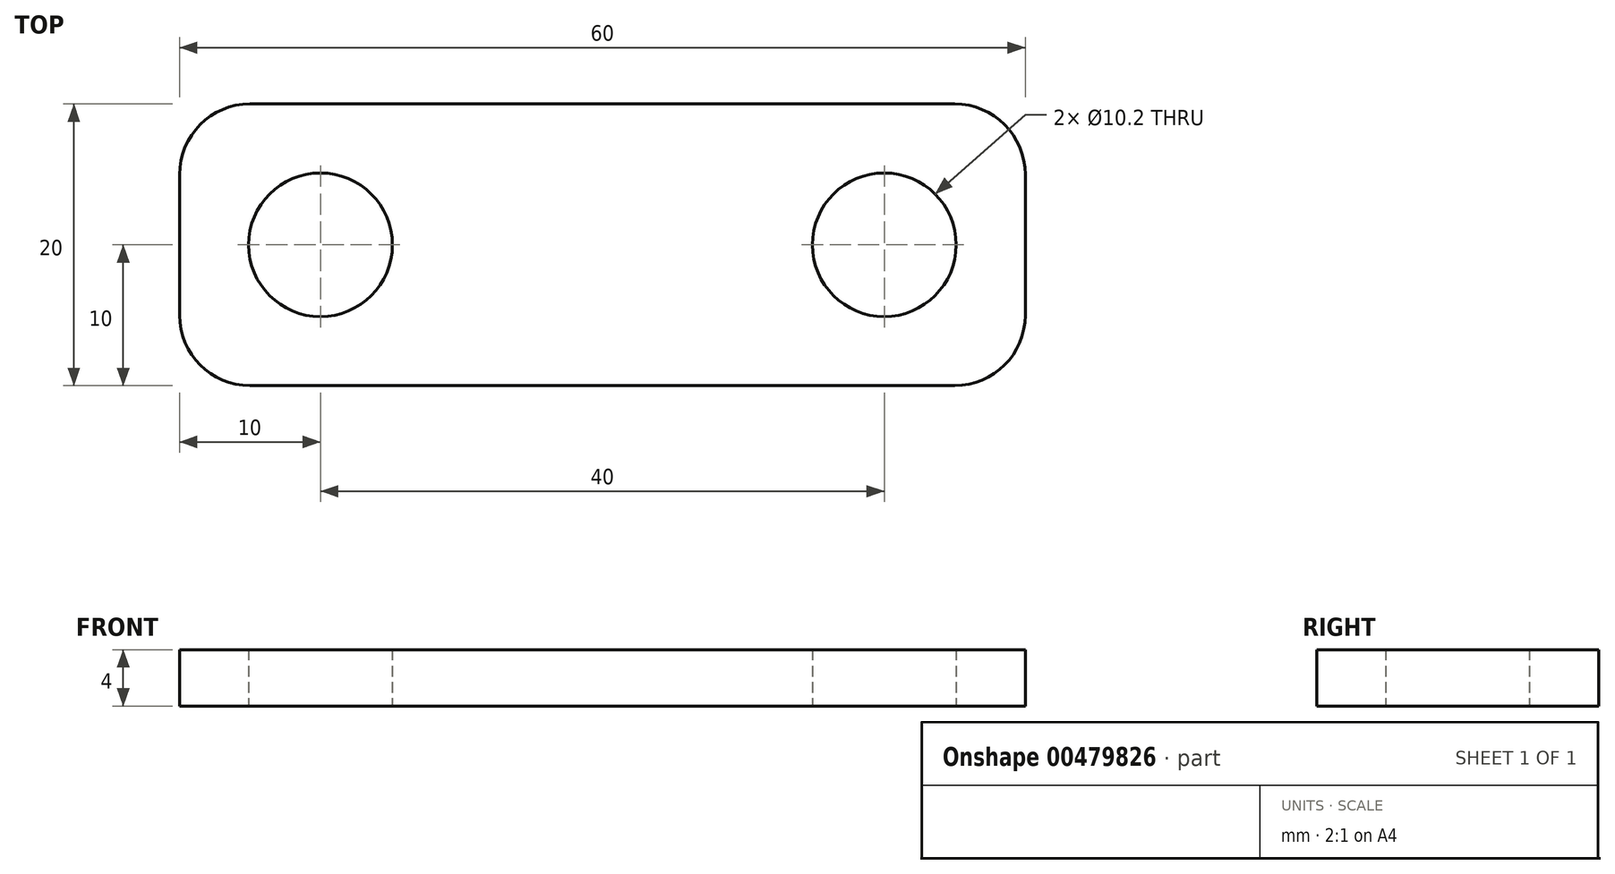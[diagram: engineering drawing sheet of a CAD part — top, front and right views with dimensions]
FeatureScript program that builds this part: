
annotation { "Feature Type Name" : "Feature", "Feature Type Description" : "" }
export const myFeature = defineFeature(function(context is Context, id is Id, definition is map)
    precondition{}
    {
        {
            var Q0;
            Q0=qCreatedBy(makeId("Top.planeOp"),FACE);
            var sketch = newSketch(context, id + "F0", { "sketchPlane" : qUnion([Q0])});
            skLineSegment(sketch, "E0.bottom", {"start": v(-30, 10) * mm, "end": v(30, 10) * mm});
            skLineSegment(sketch, "E0.top", {"start": v(-30, -10) * mm, "end": v(30, -10) * mm});
            skLineSegment(sketch, "E0.left", {"start": v(-30, 10) * mm, "end": v(-30, -10) * mm});
            skLineSegment(sketch, "E0.right", {"start": v(30, 10) * mm, "end": v(30, -10) * mm});
            skPoint(sketch, "E1", {"position": v(-30, 0) * mm});
            skPoint(sketch, "E2", {"position": v(-20, 0) * mm});
            skPoint(sketch, "E3", {"position": v(0, 10) * mm});
            skPoint(sketch, "E4", {"position": v(0, 0) * mm});
            skPoint(sketch, "E5", {"position": v(30, 0) * mm});
            skPoint(sketch, "E6", {"position": v(20, 0) * mm});
            skSolve(sketch);
        }
        {
            var Q0;
            Q0=makeQuery(id+"F0.imprint","IMPRINT",FACE,{"disambiguationData":[TD([[makeQuery(id+"F0.imprint","IMPRINT",EDGE,{"derivedFrom":sQuery(id+"F0.wireOp",EDGE,"E0.bottom")}),-1.0]])]});
            extrude(context, id + "F1", {"entities" : qUnion([Q0]), "depth" : 4 * mm});
        }
        {
            var Q0;
            Q0=sQuery(id+"F0.wireOp",VERTEX,"E2");
            var Q1;
            Q1=sQuery(id+"F0.wireOp",VERTEX,"E6");
            var Q2;
            Q2=makeQuery(id+"F1.opExtrude","SWEPT_BODY",BODY,{"disambiguationData":[OSD([sQuery(id+"F0.wireOp",EDGE,"E0.bottom"),sQuery(id+"F0.wireOp",EDGE,"E0.top"),sQuery(id+"F0.wireOp",EDGE,"E0.left"),sQuery(id+"F0.wireOp",EDGE,"E0.right")])]});
            hole(context, id + "F2", {"style" : HoleStyle.SIMPLE, "endStyle" : HoleEndStyle.THROUGH, "oppositeDirection" : true, "holeDiameter" : 10.2 * mm, "tappedDepth" : 12 * mm, "tapClearance" : 3, "locations" : qUnion([Q0, Q1]), "scope" : qUnion([Q2])});
        }
        {
            var Q0;
            Q0=makeQuery(id+"F1.opExtrude","SWEPT_EDGE",EDGE,{"disambiguationData":[OSD([sQuery(id+"F0.wireOp",EDGE,"E0.bottom"),sQuery(id+"F0.wireOp",EDGE,"E0.left")])]});
            var Q1;
            Q1=makeQuery(id+"F1.opExtrude","SWEPT_EDGE",EDGE,{"disambiguationData":[OSD([sQuery(id+"F0.wireOp",EDGE,"E0.top"),sQuery(id+"F0.wireOp",EDGE,"E0.left")])]});
            var Q2;
            Q2=makeQuery(id+"F1.opExtrude","SWEPT_EDGE",EDGE,{"disambiguationData":[OSD([sQuery(id+"F0.wireOp",EDGE,"E0.bottom"),sQuery(id+"F0.wireOp",EDGE,"E0.right")])]});
            var Q3;
            Q3=makeQuery(id+"F1.opExtrude","SWEPT_EDGE",EDGE,{"disambiguationData":[OSD([sQuery(id+"F0.wireOp",EDGE,"E0.top"),sQuery(id+"F0.wireOp",EDGE,"E0.right")])]});
            fillet(context, id + "F3", {"entities" : qUnion([Q0, Q1, Q2, Q3]), "radius" : 5 * mm, "tangentPropagation" : true, "allowEdgeOverflow" : false});
        }
    });
